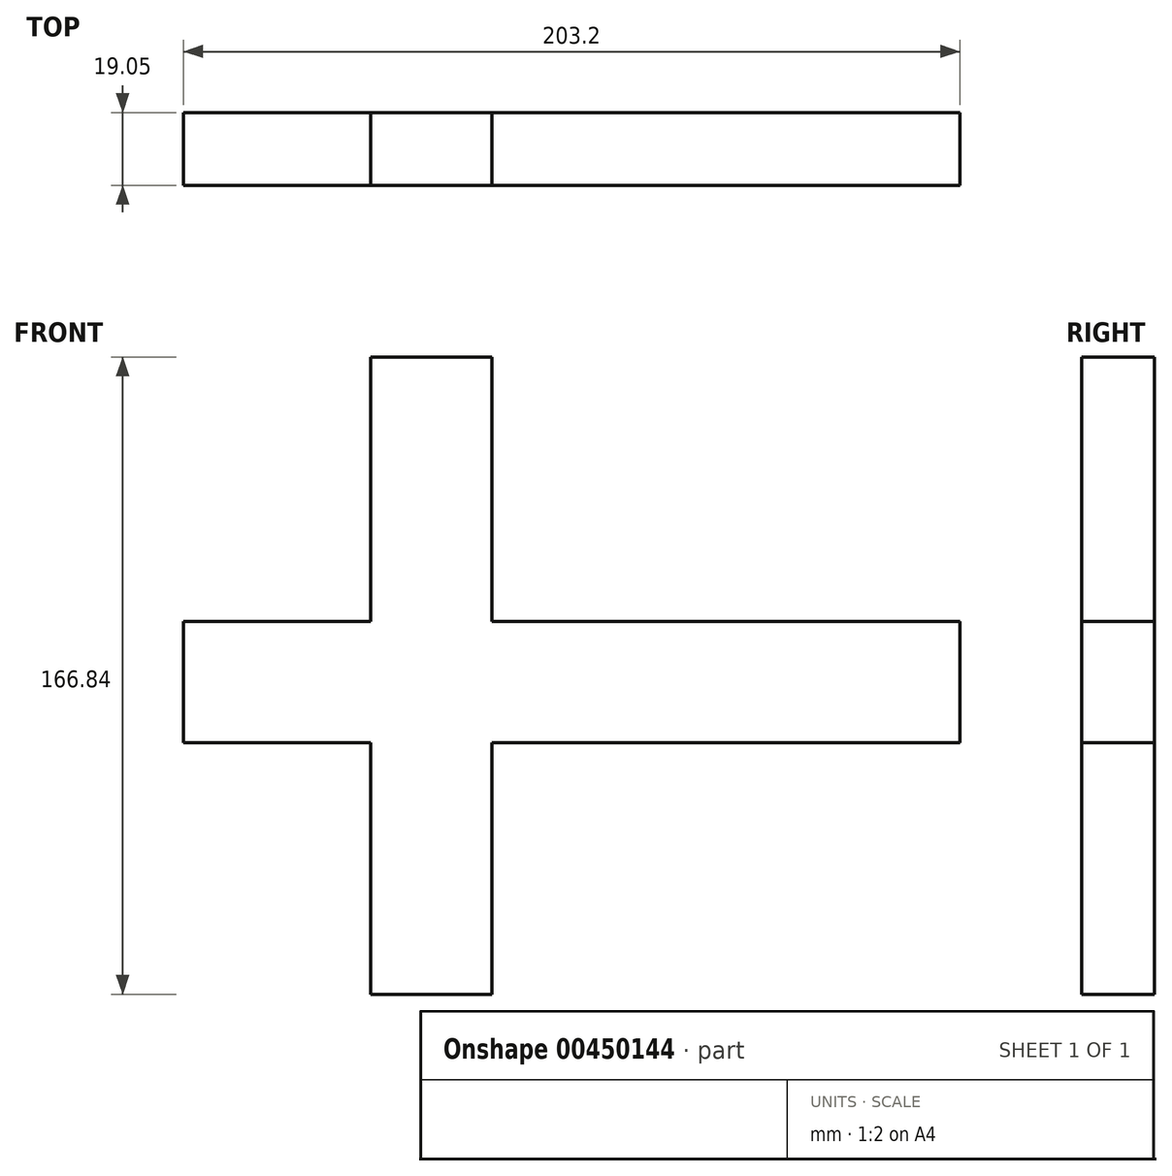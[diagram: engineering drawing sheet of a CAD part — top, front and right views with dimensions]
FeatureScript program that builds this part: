
annotation { "Feature Type Name" : "Feature", "Feature Type Description" : "" }
export const myFeature = defineFeature(function(context is Context, id is Id, definition is map)
    precondition{}
    {
        {
            var Q0;
            Q0=qCreatedBy(makeId("Front.planeOp"),FACE);
            var sketch = newSketch(context, id + "F0", { "sketchPlane" : qUnion([Q0])});
            skLineSegment(sketch, "E0.bottom", {"start": v(-151.18, 25.24) * mm, "end": v(52.02, 25.24) * mm});
            skLineSegment(sketch, "E0.top", {"start": v(-151.18, -6.5) * mm, "end": v(52.02, -6.5) * mm});
            skLineSegment(sketch, "E0.left", {"start": v(-151.18, 25.24) * mm, "end": v(-151.18, -6.5) * mm});
            skLineSegment(sketch, "E0.right", {"start": v(52.02, 25.24) * mm, "end": v(52.02, -6.5) * mm});
            skLineSegment(sketch, "E1", {"start": v(-102.22, 25.24) * mm, "end": v(-102.22, -6.5) * mm});
            skLineSegment(sketch, "E2", {"start": v(-70.47, 25.24) * mm, "end": v(-70.47, -6.5) * mm});
            skLineSegment(sketch, "E3.bottom", {"start": v(-102.22, 25.24) * mm, "end": v(-70.47, 25.24) * mm});
            skLineSegment(sketch, "E3.top", {"start": v(-102.22, 94.5) * mm, "end": v(-70.47, 94.5) * mm});
            skLineSegment(sketch, "E3.left", {"start": v(-102.22, 25.24) * mm, "end": v(-102.22, 94.5) * mm});
            skLineSegment(sketch, "E3.right", {"start": v(-70.47, 25.24) * mm, "end": v(-70.47, 94.5) * mm});
            skLineSegment(sketch, "E4.bottom", {"start": v(-102.22, -6.5) * mm, "end": v(-70.47, -6.5) * mm});
            skLineSegment(sketch, "E4.top", {"start": v(-102.22, -72.33) * mm, "end": v(-70.47, -72.33) * mm});
            skLineSegment(sketch, "E4.left", {"start": v(-102.22, -6.5) * mm, "end": v(-102.22, -72.33) * mm});
            skLineSegment(sketch, "E4.right", {"start": v(-70.47, -6.5) * mm, "end": v(-70.47, -72.33) * mm});
            skLineSegment(sketch, "E5", {"start": v(-151.18, 9.37) * mm, "end": v(52.02, 9.37) * mm});
            skLineSegment(sketch, "E6", {"start": v(-86.35, 94.5) * mm, "end": v(-86.35, -72.33) * mm});
            skSolve(sketch);
        }
        {
            var Q0;
            {var subQ0=sQuery(id+"F0.wireOp",EDGE,"E0.left");var subQ1=sQuery(id+"F0.wireOp",EDGE,"E0.bottom");var subQ2=makeQuery(id+"F0.imprint","INTERSECT",VERTEX,{"derivedFrom":[subQ1,subQ0]});Q0=makeQuery(id+"F0.imprint","IMPRINT",FACE,{"disambiguationData":[TD([[makeQuery(id+"F0.imprint","IMPRINT",EDGE,{"disambiguationData":[TD([[subQ2,-1.0]])],"derivedFrom":subQ0}),1.0]])]});}
            var Q1;
            {var subQ0=sQuery(id+"F0.wireOp",EDGE,"E0.left");var subQ1=sQuery(id+"F0.wireOp",EDGE,"E0.top");var subQ2=makeQuery(id+"F0.imprint","INTERSECT",VERTEX,{"derivedFrom":[subQ1,subQ0]});Q1=makeQuery(id+"F0.imprint","IMPRINT",FACE,{"disambiguationData":[TD([[makeQuery(id+"F0.imprint","IMPRINT",EDGE,{"disambiguationData":[TD([[subQ2,1.0]])],"derivedFrom":subQ0}),1.0]])]});}
            var Q2;
            {var subQ1=sQuery(id+"F0.wireOp",EDGE,"E1");var subQ3=sQuery(id+"F0.wireOp",EDGE,"E5");var subQ4=makeQuery(id+"F0.imprint","INTERSECT",VERTEX,{"derivedFrom":[subQ1,subQ3]});Q2=makeQuery(id+"F0.imprint","IMPRINT",FACE,{"disambiguationData":[TD([[makeQuery(id+"F0.imprint","IMPRINT",EDGE,{"disambiguationData":[TD([[subQ4,-1.0]])],"derivedFrom":subQ3}),-1.0]])]});}
            var Q3;
            {var subQ0=sQuery(id+"F0.wireOp",EDGE,"E4.left");Q3=makeQuery(id+"F0.imprint","IMPRINT",FACE,{"disambiguationData":[TD([[makeQuery(id+"F0.imprint","IMPRINT",EDGE,{"derivedFrom":subQ0}),1.0]])]});}
            var Q4;
            {var subQ0=sQuery(id+"F0.wireOp",EDGE,"E4.right");Q4=makeQuery(id+"F0.imprint","IMPRINT",FACE,{"disambiguationData":[TD([[makeQuery(id+"F0.imprint","IMPRINT",EDGE,{"derivedFrom":subQ0}),-1.0]])]});}
            var Q5;
            {var subQ1=sQuery(id+"F0.wireOp",EDGE,"E2");var subQ3=sQuery(id+"F0.wireOp",EDGE,"E5");var subQ4=makeQuery(id+"F0.imprint","INTERSECT",VERTEX,{"derivedFrom":[subQ1,subQ3]});Q5=makeQuery(id+"F0.imprint","IMPRINT",FACE,{"disambiguationData":[TD([[makeQuery(id+"F0.imprint","IMPRINT",EDGE,{"disambiguationData":[TD([[subQ4,1.0]])],"derivedFrom":subQ3}),-1.0]])]});}
            var Q6;
            {var subQ0=sQuery(id+"F0.wireOp",EDGE,"E0.right");var subQ1=sQuery(id+"F0.wireOp",EDGE,"E0.top");var subQ2=makeQuery(id+"F0.imprint","INTERSECT",VERTEX,{"derivedFrom":[subQ1,subQ0]});Q6=makeQuery(id+"F0.imprint","IMPRINT",FACE,{"disambiguationData":[TD([[makeQuery(id+"F0.imprint","IMPRINT",EDGE,{"disambiguationData":[TD([[subQ2,1.0]])],"derivedFrom":subQ0}),-1.0]])]});}
            var Q7;
            {var subQ0=sQuery(id+"F0.wireOp",EDGE,"E0.right");var subQ1=sQuery(id+"F0.wireOp",EDGE,"E0.bottom");var subQ2=makeQuery(id+"F0.imprint","INTERSECT",VERTEX,{"derivedFrom":[subQ1,subQ0]});Q7=makeQuery(id+"F0.imprint","IMPRINT",FACE,{"disambiguationData":[TD([[makeQuery(id+"F0.imprint","IMPRINT",EDGE,{"disambiguationData":[TD([[subQ2,-1.0]])],"derivedFrom":subQ0}),-1.0]])]});}
            var Q8;
            {var subQ1=sQuery(id+"F0.wireOp",EDGE,"E2");var subQ3=sQuery(id+"F0.wireOp",EDGE,"E5");var subQ4=makeQuery(id+"F0.imprint","INTERSECT",VERTEX,{"derivedFrom":[subQ1,subQ3]});Q8=makeQuery(id+"F0.imprint","IMPRINT",FACE,{"disambiguationData":[TD([[makeQuery(id+"F0.imprint","IMPRINT",EDGE,{"disambiguationData":[TD([[subQ4,1.0]])],"derivedFrom":subQ3}),1.0]])]});}
            var Q9;
            {var subQ1=sQuery(id+"F0.wireOp",EDGE,"E1");var subQ3=sQuery(id+"F0.wireOp",EDGE,"E5");var subQ4=makeQuery(id+"F0.imprint","INTERSECT",VERTEX,{"derivedFrom":[subQ1,subQ3]});Q9=makeQuery(id+"F0.imprint","IMPRINT",FACE,{"disambiguationData":[TD([[makeQuery(id+"F0.imprint","IMPRINT",EDGE,{"disambiguationData":[TD([[subQ4,-1.0]])],"derivedFrom":subQ3}),1.0]])]});}
            var Q10;
            {var subQ0=sQuery(id+"F0.wireOp",EDGE,"E3.right");Q10=makeQuery(id+"F0.imprint","IMPRINT",FACE,{"disambiguationData":[TD([[makeQuery(id+"F0.imprint","IMPRINT",EDGE,{"derivedFrom":subQ0}),1.0]])]});}
            var Q11;
            {var subQ0=sQuery(id+"F0.wireOp",EDGE,"E3.left");Q11=makeQuery(id+"F0.imprint","IMPRINT",FACE,{"disambiguationData":[TD([[makeQuery(id+"F0.imprint","IMPRINT",EDGE,{"derivedFrom":subQ0}),-1.0]])]});}
            extrude(context, id + "F1", {"entities" : qUnion([Q0, Q1, Q2, Q3, Q4, Q5, Q6, Q7, Q8, Q9, Q10, Q11]), "depth" : 19.05 * mm});
        }
    });
